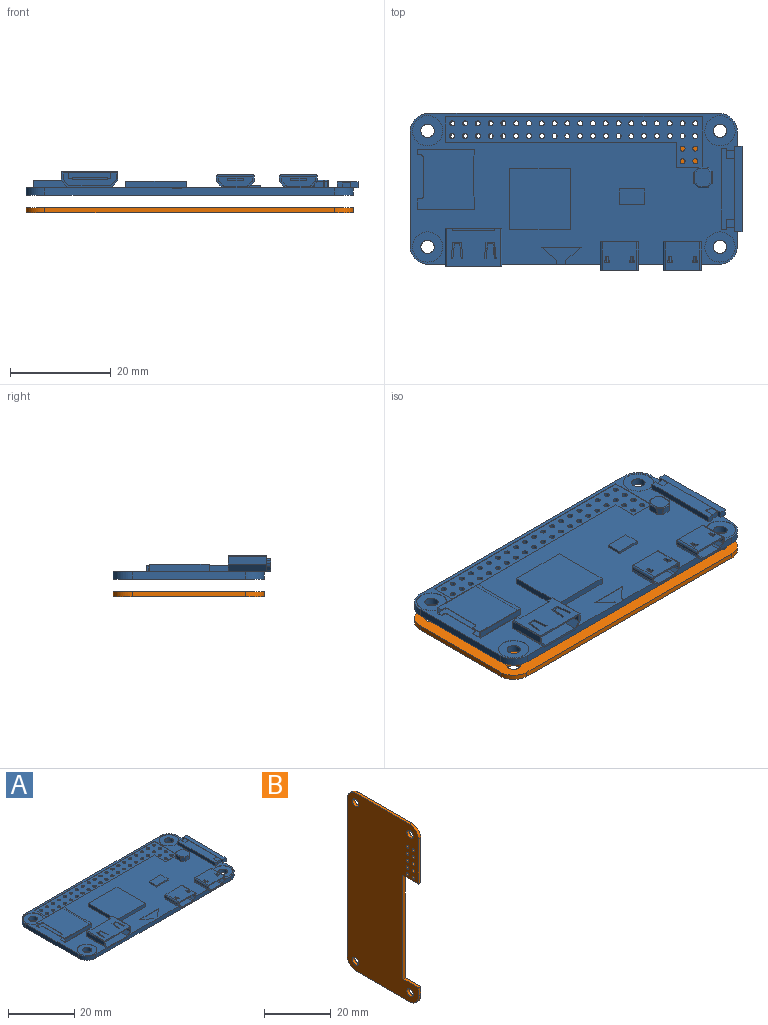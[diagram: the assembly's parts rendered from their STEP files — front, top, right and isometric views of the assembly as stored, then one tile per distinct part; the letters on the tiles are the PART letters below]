
ASSEMBLY  parts=2 mates=1
PART A: 316 faces, bbox 65.9x31.3x4.8 mm
  f0: plane 8.42x0.4mm, normal (0,0,-1), area 3.4mm2, adj f8,f9,f10,f121
  f1: plane 10.55x2.6mm, normal (0,-1,0), area 22.2mm2, adj f15,f16,f17,f18,f19,f20,f21,f22
  f2: plane 7.6x1.57mm, normal (-1,0,0), area 12mm2, adj f7,f8,f11,f13
  f3: plane 10.85x7.6mm, normal (0,0,1), area 72.9mm2, adj f7,f8,f13,f14,f26,f27,f28,f29
  f4: plane 7.6x1.57mm, normal (1,0,0), area 12mm2, adj f7,f8,f12,f14
  f5: plane 7.6x1.33mm, normal (0.74,0,-0.67), area 13.7mm2, adj f7,f8,f9,f12
  f6: plane 7.6x1.33mm, normal (-0.74,0,-0.67), area 13.7mm2, adj f7,f8,f10,f11
  f7: plane 11.25x3.3mm, normal (0,1,0), area 23.4mm2, adj f2,f3,f4,f5,f6,f9,f10,f11
  f8: plane 11.25x3.3mm, normal (0,-1,0), area 9.1mm2, adj f0,f2,f3,f4,f5,f6,f9,f10
  f9: cylinder r=0.2mm len=7.6mm, axis (0,-1,0), area 1.3mm2, adj f0,f5,f7,f8,f98
  f10: cylinder r=0.2mm len=7.6mm, axis (0,-1,0), area 1.3mm2, adj f0,f6,f7,f8,f98
  f11: cylinder r=0.2mm len=7.6mm, axis (0,-1,0), area 1.1mm2, adj f2,f6,f7,f8
  f12: cylinder r=0.2mm len=7.6mm, axis (0,-1,0), area 1.1mm2, adj f4,f5,f7,f8
  f13: cylinder r=0.2mm len=7.6mm, axis (0,-1,0), area 2.4mm2, adj f2,f3,f7,f8
  f14: cylinder r=0.2mm len=7.6mm, axis (0,-1,0), area 2.4mm2, adj f3,f4,f7,f8
  f15: plane 10.55x7mm, normal (0,0,-1), area 68.5mm2, adj f1,f8,f16,f20,f26,f27,f28,f29
  f16: plane 7x1.36mm, normal (-1,0,0), area 9.5mm2, adj f1,f8,f15,f17
  f17: plane 7x1.24mm, normal (-0.74,0,0.67), area 11.7mm2, adj f1,f8,f16,f18
  f18: plane 8.29x7mm, normal (0,0,1), area 58mm2, adj f1,f8,f17,f19
  f19: plane 7x1.24mm, normal (0.74,0,0.67), area 11.7mm2, adj f1,f8,f18,f20
  f20: plane 7x1.36mm, normal (1,0,0), area 9.5mm2, adj f1,f8,f15,f19
  f21: plane 3.5x0.55mm, normal (-1,0,0), area 1.9mm2, adj f1,f22,f24,f25
  f22: plane 7x3.5mm, normal (0,0,-1), area 24.5mm2, adj f1,f21,f23,f25
  f23: plane 3.5x0.55mm, normal (1,0,0), area 1.9mm2, adj f1,f22,f24,f25
  f24: plane 7x3.5mm, normal (0,0,1), area 24.5mm2, adj f1,f21,f23,f25
  f25: plane 7x0.55mm, normal (0,-1,0), area 3.8mm2, adj f21,f22,f23,f24
  f26: plane 3.3x0.35mm, normal (-1,-0.1,0), area 1.2mm2, adj f3,f15,f27,f33
  f27: plane 1.7x0.35mm, normal (0,-1,0), area 0.6mm2, adj f3,f15,f26,f28
  f28: plane 3.3x0.35mm, normal (1,-0.1,0), area 1.2mm2, adj f3,f15,f27,f29
  f29: plane 0.35x0.35mm, normal (0,1,0), area 0.1mm2, adj f3,f15,f28,f30
  f30: plane 2.95x0.35mm, normal (-1,0.1,0), area 1mm2, adj f3,f15,f29,f31
  f31: plane 1.07x0.35mm, normal (0,1,0), area 0.4mm2, adj f3,f15,f30,f32
  f32: plane 2.95x0.35mm, normal (1,0.1,0), area 1mm2, adj f3,f15,f31,f33
  f33: plane 0.35x0.35mm, normal (0,1,0), area 0.1mm2, adj f3,f15,f26,f32
  f34: plane 1.7x0.35mm, normal (0,-1,0), area 0.6mm2, adj f3,f15,f35,f41
  f35: plane 3.3x0.35mm, normal (1,-0.1,0), area 1.2mm2, adj f3,f15,f34,f36
  f36: plane 0.35x0.35mm, normal (0,1,0), area 0.1mm2, adj f3,f15,f35,f37
  f37: plane 2.95x0.35mm, normal (-1,0.1,0), area 1mm2, adj f3,f15,f36,f38
  f38: plane 1.07x0.35mm, normal (0,1,0), area 0.4mm2, adj f3,f15,f37,f39
  f39: plane 2.95x0.35mm, normal (1,0.1,0), area 1mm2, adj f3,f15,f38,f40
  f40: plane 0.35x0.35mm, normal (0,1,0), area 0.1mm2, adj f3,f15,f39,f41
  f41: plane 3.3x0.35mm, normal (-1,-0.1,0), area 1.2mm2, adj f3,f15,f34,f40
  f42: plane 1.4x0.5mm, normal (-1,0,0), area 0.7mm2, adj f3,f7,f44,f45
  f43: plane 1.4x0.5mm, normal (1,0,0), area 0.7mm2, adj f3,f7,f44,f45
  f44: plane 8.4x0.5mm, normal (0,0,1), area 4.2mm2, adj f7,f42,f43,f45
  f45: plane 8.4x1.4mm, normal (0,1,0), area 11.8mm2, adj f3,f42,f43,f44
  f46: cylinder r=3mm len=6mm, axis (0,0,1), area 1.9mm2, adj f98,f137
  f47: cylinder r=3mm len=6mm, axis (0,0,1), area 1.9mm2, adj f98,f136
  f48: cylinder r=3mm len=6mm, axis (0,0,1), area 1.9mm2, adj f98,f135
  f49: cylinder r=3mm len=6mm, axis (0,0,1), area 1.9mm2, adj f98,f127
  f50: cylinder r=1.32mm len=2.65mm, axis (0,0,1), area 11.7mm2, adj f126,f127
  f51: cylinder r=0.5mm len=1.4mm, axis (0,0,1), area 4.4mm2, adj f126,f128
  f52: cylinder r=0.5mm len=1.4mm, axis (0,0,1), area 4.4mm2, adj f126,f128
  f53: cylinder r=0.5mm len=1.4mm, axis (0,0,1), area 4.4mm2, adj f126,f128
  f54: cylinder r=0.5mm len=1.4mm, axis (0,0,1), area 4.4mm2, adj f126,f128
  f55: cylinder r=0.5mm len=1.4mm, axis (0,0,1), area 4.4mm2, adj f126,f128
  f56: cylinder r=0.5mm len=1.4mm, axis (0,0,1), area 4.4mm2, adj f126,f128
  f57: cylinder r=0.5mm len=1.4mm, axis (0,0,1), area 4.4mm2, adj f126,f128
  f58: cylinder r=0.5mm len=1.4mm, axis (0,0,1), area 4.4mm2, adj f126,f128
  f59: cylinder r=1.32mm len=2.65mm, axis (0,0,1), area 11.7mm2, adj f126,f135
  f60: cylinder r=1.32mm len=2.65mm, axis (0,0,1), area 11.7mm2, adj f126,f136
  f61: cylinder r=1.32mm len=2.65mm, axis (0,0,1), area 11.7mm2, adj f126,f137
  f62: cylinder r=0.5mm len=1.4mm, axis (0,0,1), area 4.4mm2, adj f126,f128
  f63: cylinder r=0.5mm len=1.4mm, axis (0,0,1), area 4.4mm2, adj f126,f128
  f64: cylinder r=0.5mm len=1.4mm, axis (0,0,1), area 4.4mm2, adj f126,f128
  f65: cylinder r=0.5mm len=1.4mm, axis (0,0,1), area 4.4mm2, adj f126,f128
  f66: cylinder r=0.5mm len=1.4mm, axis (0,0,1), area 4.4mm2, adj f126,f128
  f67: cylinder r=0.5mm len=1.4mm, axis (0,0,1), area 4.4mm2, adj f126,f128
  f68: cylinder r=0.5mm len=1.4mm, axis (0,0,1), area 4.4mm2, adj f126,f128
  f69: cylinder r=0.5mm len=1.4mm, axis (0,0,1), area 4.4mm2, adj f126,f128
  f70: cylinder r=0.5mm len=1.4mm, axis (0,0,1), area 4.4mm2, adj f126,f128
  f71: cylinder r=0.5mm len=1.4mm, axis (0,0,1), area 4.4mm2, adj f126,f128
  f72: cylinder r=0.5mm len=1.4mm, axis (0,0,1), area 4.4mm2, adj f126,f128
  f73: cylinder r=0.5mm len=1.4mm, axis (0,0,1), area 4.4mm2, adj f126,f128
  f74: cylinder r=0.5mm len=1.4mm, axis (0,0,1), area 4.4mm2, adj f126,f128
  f75: cylinder r=0.5mm len=1.4mm, axis (0,0,1), area 4.4mm2, adj f126,f128
  f76: cylinder r=0.5mm len=1.4mm, axis (0,0,1), area 4.4mm2, adj f126,f128
  f77: cylinder r=0.5mm len=1.4mm, axis (0,0,1), area 4.4mm2, adj f126,f128
  f78: cylinder r=0.5mm len=1.4mm, axis (0,0,1), area 4.4mm2, adj f126,f128
  f79: cylinder r=0.5mm len=1.4mm, axis (0,0,1), area 4.4mm2, adj f126,f128
  f80: cylinder r=0.5mm len=1.4mm, axis (0,0,1), area 4.4mm2, adj f126,f128
  f81: cylinder r=0.5mm len=1.4mm, axis (0,0,1), area 4.4mm2, adj f126,f128
  f82: cylinder r=0.5mm len=1.4mm, axis (0,0,1), area 4.4mm2, adj f126,f128
  f83: cylinder r=0.5mm len=1.4mm, axis (0,0,1), area 4.4mm2, adj f126,f128
  f84: cylinder r=0.5mm len=1.4mm, axis (0,0,1), area 4.4mm2, adj f126,f128
  f85: cylinder r=0.5mm len=1.4mm, axis (0,0,1), area 4.4mm2, adj f126,f128
  f86: cylinder r=0.5mm len=1.4mm, axis (0,0,1), area 4.4mm2, adj f126,f128
  f87: cylinder r=0.5mm len=1.4mm, axis (0,0,1), area 4.4mm2, adj f126,f128
  f88: cylinder r=0.5mm len=1.4mm, axis (0,0,1), area 4.4mm2, adj f126,f128
  f89: cylinder r=0.5mm len=1.4mm, axis (0,0,1), area 4.4mm2, adj f126,f128
  f90: cylinder r=0.5mm len=1.4mm, axis (0,0,1), area 4.4mm2, adj f126,f128
  f91: cylinder r=0.5mm len=1.4mm, axis (0,0,1), area 4.4mm2, adj f126,f128
  f92: cylinder r=0.5mm len=1.4mm, axis (0,0,1), area 4.4mm2, adj f126,f128
  f93: cylinder r=0.5mm len=1.4mm, axis (0,0,1), area 4.4mm2, adj f126,f128
  f94: cylinder r=0.5mm len=1.4mm, axis (0,0,1), area 4.4mm2, adj f126,f128
  f95: cylinder r=0.5mm len=1.4mm, axis (0,0,1), area 4.4mm2, adj f126,f128
  f96: cylinder r=0.5mm len=1.4mm, axis (0,0,1), area 4.4mm2, adj f126,f128
  f97: cylinder r=0.5mm len=1.4mm, axis (0,0,1), area 4.4mm2, adj f126,f128
  f98: plane 65x30mm, normal (0,0,1), area 1077.1mm2, adj f7,f9,f10,f46,f47,f48,f49,f99
  f99: plane 17x1.2mm, normal (-1,0,0), area 2.7mm2, adj f98,f102,f258,f259,f260,f267,f268,f273
  f100: plane 2x1.19mm, normal (1,0,0), area 0.7mm2, adj f98,f267,f268,f269,f275,f276
  f101: plane 2x1.19mm, normal (1,0,0), area 0.7mm2, adj f98,f102,f267,f271,f273,f274
  f102: plane 1.6x0.19mm, normal (0,1,0), area 0.3mm2, adj f99,f101,f267,f274
  f103: plane 11.9x0.5mm, normal (0,0,1), area 6mm2, adj f123,f262,f264,f272
  f104: plane 6.91x1.96mm, normal (0,-1,0), area 11.2mm2, adj f204,f205,f206,f207,f208,f209,f210,f211
  f105: plane 6.91x1.96mm, normal (0,-1,0), area 11.2mm2, adj f192,f193,f194,f195,f196,f197,f198,f199
  f106: plane 1.45x1.1mm, normal (-1,0,0), area 0.3mm2, adj f98,f107,f108,f155,f156,f157,f159,f160
  f107: plane 0.65x0.1mm, normal (0,-1,0), area 0.1mm2, adj f98,f106,f109,f160
  f108: plane 0.65x0.1mm, normal (0,-1,0), area 0.1mm2, adj f106,f110,f156,f162
  f109: cylinder r=0.5mm len=0.5mm, axis (0,0,-1), area 0.1mm2, adj f98,f107,f111,f160
  f110: cylinder r=0.5mm len=0.5mm, axis (0,0,-1), area 0.1mm2, adj f108,f112,f156,f162
  f111: plane 7.75x0.1mm, normal (-1,0,0), area 0.8mm2, adj f98,f109,f113,f160
  f112: plane 7.75x0.1mm, normal (-1,0,0), area 0.8mm2, adj f110,f114,f156,f162
  f113: cylinder r=0.5mm len=0.5mm, axis (0,0,-1), area 0.1mm2, adj f98,f111,f115,f160
  f114: cylinder r=0.5mm len=0.5mm, axis (0,0,-1), area 0.1mm2, adj f112,f116,f156,f162
  f115: plane 0.65x0.1mm, normal (0,1,0), area 0.1mm2, adj f98,f113,f117,f160
  f116: plane 0.65x0.1mm, normal (0,1,0), area 0.1mm2, adj f114,f117,f156,f162
  f117: plane 2.15x1.45mm, normal (-1,0,0), area 0.6mm2, adj f98,f115,f116,f149,f156,f158,f160,f161
  f118: cylinder r=3.75mm len=3.75mm, axis (0,0,-1), area 8.8mm2, adj f98,f119,f125,f126
  f119: plane 22.5x1.5mm, normal (-1,0,0), area 33.8mm2, adj f98,f118,f120,f126
  f120: cylinder r=3.75mm len=3.75mm, axis (0,0,-1), area 8.8mm2, adj f98,f119,f121,f126
  f121: plane 57.5x1.5mm, normal (0,-1,0), area 86.1mm2, adj f0,f98,f120,f122,f126,f141,f142,f143
  f122: cylinder r=3.75mm len=3.75mm, axis (0,0,-1), area 8.8mm2, adj f98,f121,f123,f126
  f123: plane 22.5x1.5mm, normal (1,0,0), area 33.8mm2, adj f98,f103,f122,f124,f126,f261,f265
  f124: cylinder r=3.75mm len=3.75mm, axis (0,0,-1), area 8.8mm2, adj f98,f123,f125,f126
  f125: plane 57.5x1.5mm, normal (0,1,0), area 86.3mm2, adj f98,f118,f124,f126
  f126: plane 65x30mm, normal (0,0,-1), area 1881.3mm2, adj f50,f51,f52,f53,f54,f55,f56,f57
  f127: plane 6x6mm, normal (0,0,1), area 22.8mm2, adj f49,f50
  f128: plane 51x10.1mm, normal (0,0,1), area 251mm2, adj f51,f52,f53,f54,f55,f56,f57,f58
  f129: plane 5.1x0.1mm, normal (1,0,0), area 0.5mm2, adj f98,f128,f130,f134
  f130: plane 51x0.1mm, normal (0,-1,0), area 5.1mm2, adj f98,f128,f129,f131
  f131: plane 10.1x0.1mm, normal (-1,0,0), area 1mm2, adj f98,f128,f130,f132,f277
  f132: plane 5.1x0.1mm, normal (0,1,0), area 0.5mm2, adj f98,f128,f131,f133,f277
  f133: plane 5x0.1mm, normal (1,0,0), area 0.5mm2, adj f98,f128,f132,f134
  f134: plane 45.9x0.1mm, normal (0,1,0), area 4.6mm2, adj f98,f128,f129,f133
  f135: plane 6x6mm, normal (0,0,1), area 22.8mm2, adj f48,f59
  f136: plane 6x6mm, normal (0,0,1), area 22.8mm2, adj f47,f60
  f137: plane 6x6mm, normal (0,0,1), area 22.8mm2, adj f46,f61
  f138: plane 3.08x2.65mm, normal (0.65,0.76,0), area 0.4mm2, adj f98,f139,f142,f143
  f139: plane 8x0.1mm, normal (0,-1,0), area 0.8mm2, adj f98,f138,f140,f143
  f140: plane 3.08x2.65mm, normal (-0.65,0.76,0), area 0.4mm2, adj f98,f139,f141,f143
  f141: plane 0.8x0.1mm, normal (-1,0,0), area 0.1mm2, adj f98,f121,f140,f143
  f142: plane 0.8x0.1mm, normal (1,0,0), area 0.1mm2, adj f98,f121,f138,f143
  f143: plane 8x3.45mm, normal (0,0,1), area 14.5mm2, adj f121,f138,f139,f140,f141,f142
  f144: plane 12x1.25mm, normal (1,0,0), area 15mm2, adj f98,f145,f147,f148
  f145: plane 12x1.25mm, normal (0,1,0), area 15mm2, adj f98,f144,f146,f148
  f146: plane 12x1.25mm, normal (-1,0,0), area 15mm2, adj f98,f145,f147,f148
  f147: plane 12x1.25mm, normal (0,-1,0), area 15mm2, adj f98,f144,f146,f148
  f148: plane 12x12mm, normal (0,0,1), area 144mm2, adj f144,f145,f146,f147
  f149: plane 11.4x1.35mm, normal (0,-1,0), area 15.4mm2, adj f98,f117,f150,f158
  f150: plane 2.5x1.45mm, normal (1,0,0), area 3.6mm2, adj f98,f149,f151,f156,f158
  f151: plane 1.45x0.25mm, normal (0.71,0.71,0), area 0.5mm2, adj f98,f150,f152,f156
  f152: plane 7.9x1.45mm, normal (1,0,0), area 11.5mm2, adj f98,f151,f153,f156
  f153: plane 1.45x0.25mm, normal (0.71,-0.71,0), area 0.5mm2, adj f98,f152,f154,f156
  f154: plane 1.45x1.1mm, normal (1,0,0), area 1.6mm2, adj f98,f153,f155,f156,f157
  f155: plane 11.4x1.35mm, normal (0,1,0), area 15.4mm2, adj f98,f106,f154,f157
  f156: plane 11.8x11.4mm, normal (0,0,1), area 122.5mm2, adj f106,f108,f110,f112,f114,f116,f117,f150
  f157: cylinder r=0.1mm len=11.4mm, axis (-1,0,0), area 1.8mm2, adj f106,f154,f155,f156
  f158: cylinder r=0.1mm len=11.4mm, axis (1,0,0), area 1.8mm2, adj f117,f149,f150,f156
  f159: plane 10.65x1.25mm, normal (0,-1,0), area 13.3mm2, adj f106,f160,f162,f163
  f160: plane 11.8x10.65mm, normal (0,0,1), area 115.7mm2, adj f106,f107,f109,f111,f113,f115,f117,f159
  f161: plane 10.65x1.25mm, normal (0,1,0), area 13.3mm2, adj f117,f160,f162,f163
  f162: plane 11.8x10.65mm, normal (0,0,-1), area 115.7mm2, adj f106,f108,f110,f112,f114,f116,f117,f159
  f163: plane 11.8x1.25mm, normal (-1,0,0), area 14.7mm2, adj f159,f160,f161,f162
  f164: plane 4.3x1.25mm, normal (0,0,-1), area 5.4mm2, adj f121,f165,f166,f177
  f165: cylinder r=1mm len=5.75mm, axis (0,-1,0), area 4.6mm2, adj f98,f164,f175,f176,f177
  f166: cylinder r=1mm len=5.75mm, axis (0,-1,0), area 4.6mm2, adj f98,f164,f167,f176,f177
  f167: plane 5.75x0.65mm, normal (-0.72,0,-0.69), area 5.2mm2, adj f166,f168,f176,f177
  f168: cylinder r=1mm len=5.75mm, axis (0,-1,0), area 4.4mm2, adj f167,f169,f176,f177
  f169: plane 5.75x0.55mm, normal (-1,0,0), area 3.1mm2, adj f168,f170,f176,f177
  f170: cylinder r=0.4mm len=5.75mm, axis (0,-1,0), area 3.6mm2, adj f169,f171,f176,f177
  f171: plane 6.75x5.75mm, normal (0,0,1), area 36.8mm2, adj f170,f172,f176,f177,f234,f235,f236,f237
  f172: cylinder r=0.4mm len=5.75mm, axis (0,-1,0), area 3.6mm2, adj f171,f173,f176,f177
  f173: plane 5.75x0.55mm, normal (1,0,0), area 3.1mm2, adj f172,f174,f176,f177
  f174: cylinder r=1mm len=5.75mm, axis (0,-1,0), area 4.4mm2, adj f173,f175,f176,f177
  f175: plane 5.75x0.65mm, normal (0.72,0,-0.69), area 5.2mm2, adj f165,f174,f176,f177
  f176: plane 7.55x2.6mm, normal (0,1,0), area 18mm2, adj f98,f165,f166,f167,f168,f169,f170,f171
  f177: plane 7.55x2.6mm, normal (0,-1,0), area 5.6mm2, adj f164,f165,f166,f167,f168,f169,f170,f171
  f178: plane 4.3x1.25mm, normal (0,0,-1), area 5.4mm2, adj f121,f183,f184,f191
  f179: cylinder r=0.4mm len=5.75mm, axis (0,-1,0), area 3.6mm2, adj f180,f189,f190,f191
  f180: plane 5.75x0.55mm, normal (1,0,0), area 3.1mm2, adj f179,f181,f190,f191
  f181: cylinder r=1mm len=5.75mm, axis (0,-1,0), area 4.4mm2, adj f180,f182,f190,f191
  f182: plane 5.75x0.65mm, normal (0.72,0,-0.69), area 5.2mm2, adj f181,f183,f190,f191
  f183: cylinder r=1mm len=5.75mm, axis (0,-1,0), area 4.6mm2, adj f98,f178,f182,f190,f191
  f184: cylinder r=1mm len=5.75mm, axis (0,-1,0), area 4.6mm2, adj f98,f178,f185,f190,f191
  f185: plane 5.75x0.65mm, normal (-0.72,0,-0.69), area 5.2mm2, adj f184,f186,f190,f191
  f186: cylinder r=1mm len=5.75mm, axis (0,-1,0), area 4.4mm2, adj f185,f187,f190,f191
  f187: plane 5.75x0.55mm, normal (-1,0,0), area 3.1mm2, adj f186,f188,f190,f191
  f188: cylinder r=0.4mm len=5.75mm, axis (0,-1,0), area 3.6mm2, adj f187,f189,f190,f191
  f189: plane 6.75x5.75mm, normal (0,0,1), area 36.8mm2, adj f179,f188,f190,f191,f226,f227,f228,f229
  f190: plane 7.55x2.6mm, normal (0,1,0), area 18mm2, adj f98,f179,f180,f181,f182,f183,f184,f185
  f191: plane 7.55x2.6mm, normal (0,-1,0), area 5.6mm2, adj f178,f179,f180,f181,f182,f183,f184,f185
  f192: cylinder r=0.08mm len=5.25mm, axis (0,-1,0), area 0.7mm2, adj f105,f191,f193,f203
  f193: plane 5.25x0.55mm, normal (-1,0,0), area 2.9mm2, adj f105,f191,f192,f194
  f194: cylinder r=0.68mm len=5.25mm, axis (0,-1,0), area 2.7mm2, adj f105,f191,f193,f195
  f195: plane 5.25x0.65mm, normal (-0.72,0,0.69), area 4.7mm2, adj f105,f191,f194,f196
  f196: cylinder r=0.68mm len=5.25mm, axis (0,-1,0), area 2.9mm2, adj f105,f191,f195,f197
  f197: plane 5.25x4.3mm, normal (0,0,1), area 22.6mm2, adj f105,f191,f196,f198
  f198: cylinder r=0.68mm len=5.25mm, axis (0,-1,0), area 2.9mm2, adj f105,f191,f197,f199
  f199: plane 5.25x0.65mm, normal (0.72,0,0.69), area 4.7mm2, adj f105,f191,f198,f200
  f200: cylinder r=0.68mm len=5.25mm, axis (0,-1,0), area 2.7mm2, adj f105,f191,f199,f201
  f201: plane 5.25x0.55mm, normal (1,0,0), area 2.9mm2, adj f105,f191,f200,f202
  f202: cylinder r=0.08mm len=5.25mm, axis (0,-1,0), area 0.7mm2, adj f105,f191,f201,f203
  f203: plane 6.75x5.25mm, normal (0,0,-1), area 33.4mm2, adj f105,f191,f192,f202,f226,f227,f228,f229
  f204: cylinder r=0.68mm len=5.25mm, axis (0,-1,0), area 2.9mm2, adj f104,f177,f205,f215
  f205: plane 5.25x4.3mm, normal (0,0,1), area 22.6mm2, adj f104,f177,f204,f206
  f206: cylinder r=0.68mm len=5.25mm, axis (0,-1,0), area 2.9mm2, adj f104,f177,f205,f207
  f207: plane 5.25x0.65mm, normal (0.72,0,0.69), area 4.7mm2, adj f104,f177,f206,f208
  f208: cylinder r=0.68mm len=5.25mm, axis (0,-1,0), area 2.7mm2, adj f104,f177,f207,f209
  f209: plane 5.25x0.55mm, normal (1,0,0), area 2.9mm2, adj f104,f177,f208,f210
  f210: cylinder r=0.08mm len=5.25mm, axis (0,-1,0), area 0.7mm2, adj f104,f177,f209,f211
  f211: plane 6.75x5.25mm, normal (0,0,-1), area 33.4mm2, adj f104,f177,f210,f212,f234,f235,f236,f237
  f212: cylinder r=0.08mm len=5.25mm, axis (0,-1,0), area 0.7mm2, adj f104,f177,f211,f213
  f213: plane 5.25x0.55mm, normal (-1,0,0), area 2.9mm2, adj f104,f177,f212,f214
  f214: cylinder r=0.68mm len=5.25mm, axis (0,-1,0), area 2.7mm2, adj f104,f177,f213,f215
  f215: plane 5.25x0.65mm, normal (-0.72,0,0.69), area 4.7mm2, adj f104,f177,f204,f214
  f216: plane 3.5x0.4mm, normal (1,0,0), area 1.4mm2, adj f105,f217,f219,f220
  f217: plane 3.5x3.15mm, normal (0,0,1), area 11mm2, adj f105,f216,f218,f220
  f218: plane 3.5x0.4mm, normal (-1,0,0), area 1.4mm2, adj f105,f217,f219,f220
  f219: plane 3.5x3.15mm, normal (0,0,-1), area 11mm2, adj f105,f216,f218,f220
  f220: plane 3.15x0.4mm, normal (0,-1,0), area 1.3mm2, adj f216,f217,f218,f219
  f221: plane 3.5x0.4mm, normal (1,0,0), area 1.4mm2, adj f104,f222,f224,f225
  f222: plane 3.5x3.15mm, normal (0,0,1), area 11mm2, adj f104,f221,f223,f225
  f223: plane 3.5x0.4mm, normal (-1,0,0), area 1.4mm2, adj f104,f222,f224,f225
  f224: plane 3.5x3.15mm, normal (0,0,-1), area 11mm2, adj f104,f221,f223,f225
  f225: plane 3.15x0.4mm, normal (0,-1,0), area 1.3mm2, adj f221,f222,f223,f224
  f226: plane 0.45x0.32mm, normal (-1,0,0), area 0.1mm2, adj f189,f203,f227,f233
  f227: plane 1.05x0.32mm, normal (0,1,0), area 0.3mm2, adj f189,f203,f226,f228
  f228: plane 0.45x0.32mm, normal (1,0,0), area 0.1mm2, adj f189,f203,f227,f229
  f229: plane 0.32x0.23mm, normal (0,-1,0), area 0.1mm2, adj f189,f203,f228,f230
  f230: plane 0.9x0.32mm, normal (1,0,0), area 0.3mm2, adj f189,f203,f229,f231
  f231: plane 0.6x0.32mm, normal (0,-1,0), area 0.2mm2, adj f189,f203,f230,f232
  f232: plane 0.9x0.32mm, normal (-1,0,0), area 0.3mm2, adj f189,f203,f231,f233
  f233: plane 0.32x0.23mm, normal (0,-1,0), area 0.1mm2, adj f189,f203,f226,f232
  f234: plane 0.6x0.32mm, normal (0,-1,0), area 0.2mm2, adj f171,f211,f235,f241
  f235: plane 0.9x0.32mm, normal (-1,0,0), area 0.3mm2, adj f171,f211,f234,f236
  f236: plane 0.32x0.23mm, normal (0,-1,0), area 0.1mm2, adj f171,f211,f235,f237
  f237: plane 0.45x0.32mm, normal (-1,0,0), area 0.1mm2, adj f171,f211,f236,f238
  f238: plane 1.05x0.32mm, normal (0,1,0), area 0.3mm2, adj f171,f211,f237,f239
  f239: plane 0.45x0.32mm, normal (1,0,0), area 0.1mm2, adj f171,f211,f238,f240
  f240: plane 0.32x0.23mm, normal (0,-1,0), area 0.1mm2, adj f171,f211,f239,f241
  f241: plane 0.9x0.32mm, normal (1,0,0), area 0.3mm2, adj f171,f211,f234,f240
  f242: plane 0.9x0.32mm, normal (-1,0,0), area 0.3mm2, adj f171,f211,f243,f249
  f243: plane 0.32x0.23mm, normal (0,-1,0), area 0.1mm2, adj f171,f211,f242,f244
  f244: plane 0.45x0.32mm, normal (-1,0,0), area 0.1mm2, adj f171,f211,f243,f245
  f245: plane 1.05x0.32mm, normal (0,1,0), area 0.3mm2, adj f171,f211,f244,f246
  f246: plane 0.45x0.32mm, normal (1,0,0), area 0.1mm2, adj f171,f211,f245,f247
  f247: plane 0.32x0.23mm, normal (0,-1,0), area 0.1mm2, adj f171,f211,f246,f248
  f248: plane 0.9x0.32mm, normal (1,0,0), area 0.3mm2, adj f171,f211,f247,f249
  f249: plane 0.6x0.32mm, normal (0,-1,0), area 0.2mm2, adj f171,f211,f242,f248
  f250: plane 0.6x0.32mm, normal (0,-1,0), area 0.2mm2, adj f189,f203,f251,f257
  f251: plane 0.9x0.32mm, normal (-1,0,0), area 0.3mm2, adj f189,f203,f250,f252
  f252: plane 0.32x0.23mm, normal (0,-1,0), area 0.1mm2, adj f189,f203,f251,f253
  f253: plane 0.45x0.32mm, normal (-1,0,0), area 0.1mm2, adj f189,f203,f252,f254
  f254: plane 1.05x0.32mm, normal (0,1,0), area 0.3mm2, adj f189,f203,f253,f255
  f255: plane 0.45x0.32mm, normal (1,0,0), area 0.1mm2, adj f189,f203,f254,f256
  f256: plane 0.32x0.23mm, normal (0,-1,0), area 0.1mm2, adj f189,f203,f255,f257
  f257: plane 0.9x0.32mm, normal (1,0,0), area 0.3mm2, adj f189,f203,f250,f256
  f258: plane 1.4x1.2mm, normal (0,-1,0), area 1.7mm2, adj f98,f99,f259,f265,f266
  f259: plane 17x1.4mm, normal (0,0,1), area 23.8mm2, adj f99,f258,f260,f266
  f260: plane 1.4x1.2mm, normal (0,1,0), area 1.7mm2, adj f98,f99,f259,f261,f266
  f261: plane 2.55x0.9mm, normal (0,0,-1), area 2.3mm2, adj f123,f260,f262,f266
  f262: plane 1.4x0.65mm, normal (0,-1,0), area 0.9mm2, adj f103,f261,f263,f266,f272
  f263: plane 11.9x1.4mm, normal (0,0,-1), area 16.7mm2, adj f262,f264,f266,f272
  f264: plane 1.4x0.65mm, normal (0,1,0), area 0.9mm2, adj f103,f263,f265,f266,f272
  f265: plane 2.55x0.9mm, normal (0,0,-1), area 2.3mm2, adj f123,f258,f264,f266
  f266: plane 17x1.2mm, normal (1,0,0), area 12.7mm2, adj f258,f259,f260,f261,f262,f263,f264,f265
  f267: plane 16x2.7mm, normal (0,0,1), area 36.8mm2, adj f99,f100,f101,f102,f268,f269,f270,f271
  f268: plane 1.6x0.19mm, normal (0,-1,0), area 0.3mm2, adj f99,f100,f267,f276
  f269: plane 1.19x1.1mm, normal (0,-1,0), area 1.3mm2, adj f98,f100,f267,f270
  f270: plane 16x1.19mm, normal (-1,0,0), area 19mm2, adj f98,f267,f269,f271
  f271: plane 1.19x1.1mm, normal (0,1,0), area 1.3mm2, adj f98,f101,f267,f270
  f272: plane 11.9x0.65mm, normal (1,0,0), area 7.7mm2, adj f103,f262,f263,f264
  f273: plane 1.6x1mm, normal (0,1,0), area 1.6mm2, adj f98,f99,f101,f274
  f274: plane 1.7x1.6mm, normal (0,0,1), area 2.7mm2, adj f99,f101,f102,f273
  f275: plane 1.6x1mm, normal (0,-1,0), area 1.6mm2, adj f98,f99,f100,f276
  f276: plane 1.7x1.6mm, normal (0,0,1), area 2.7mm2, adj f99,f100,f268,f275
  f277: plane 0.8x0.05mm, normal (0,0,-1), area 0mm2, adj f131,f132,f281,f306
  f278: plane 2.03x1.3mm, normal (-1,0,0), area 2.6mm2, adj f98,f294,f299,f300
  f279: plane 1.68x1.3mm, normal (0,-1,0), area 2.2mm2, adj f98,f292,f297,f298
  f280: plane 2.03x1.3mm, normal (1,0,0), area 2.6mm2, adj f98,f303,f309,f310
  f281: plane 1.68x1.3mm, normal (0,1,0), area 2.2mm2, adj f98,f277,f306,f311,f312
  f282: plane 3.6x3.25mm, normal (0,0,1), area 10.5mm2, adj f293,f298,f299,f304,f305,f310,f311,f315
  f283: plane 1.3x0.78mm, normal (-0.71,0.71,0), area 1.4mm2, adj f98,f300,f305,f306
  f284: plane 1.3x0.78mm, normal (0.71,0.71,0), area 1.4mm2, adj f98,f309,f312,f315
  f285: plane 1.3x0.78mm, normal (0.71,-0.71,0), area 1.4mm2, adj f98,f297,f303,f304
  f286: plane 1.3x0.78mm, normal (-0.71,-0.71,0), area 1.4mm2, adj f98,f292,f293,f294
  f287: plane 3.15x0.5mm, normal (-1,0,0), area 1.6mm2, adj f98,f288,f290,f291
  f288: plane 5x0.5mm, normal (0,-1,0), area 2.5mm2, adj f98,f287,f289,f291
  f289: plane 3.15x0.5mm, normal (1,0,0), area 1.6mm2, adj f98,f288,f290,f291
  f290: plane 5x0.5mm, normal (0,1,0), area 2.5mm2, adj f98,f287,f289,f291
  f291: plane 5x3.15mm, normal (0,0,1), area 15.7mm2, adj f287,f288,f289,f290
  f292: cylinder r=0.2mm len=1.3mm, axis (0,0,-1), area 0.2mm2, adj f98,f279,f286,f295
  f293: cylinder r=0.2mm len=0.92mm, axis (-0.71,0.71,0), area 0.3mm2, adj f282,f286,f295,f296
  f294: cylinder r=0.2mm len=1.3mm, axis (0,0,1), area 0.2mm2, adj f98,f278,f286,f296
  f295: sphere r=0.2mm, area 0mm2, adj f292,f293,f298
  f296: sphere r=0.2mm, area 0mm2, adj f293,f294,f299
  f297: cylinder r=0.2mm len=1.3mm, axis (0,0,1), area 0.2mm2, adj f98,f279,f285,f301
  f298: cylinder r=0.2mm len=1.68mm, axis (-1,0,0), area 0.5mm2, adj f279,f282,f295,f301
  f299: cylinder r=0.2mm len=2.03mm, axis (0,1,0), area 0.6mm2, adj f278,f282,f296,f302
  f300: cylinder r=0.2mm len=1.3mm, axis (0,0,-1), area 0.2mm2, adj f98,f278,f283,f302
  f301: sphere r=0.2mm, area 0mm2, adj f297,f298,f304
  f302: sphere r=0.2mm, area 0mm2, adj f299,f300,f305
  f303: cylinder r=0.2mm len=1.3mm, axis (0,0,-1), area 0.2mm2, adj f98,f280,f285,f307
  f304: cylinder r=0.2mm len=0.92mm, axis (-0.71,-0.71,0), area 0.3mm2, adj f282,f285,f301,f307
  f305: cylinder r=0.2mm len=0.92mm, axis (0.71,0.71,0), area 0.3mm2, adj f282,f283,f302,f308
  f306: cylinder r=0.2mm len=1.3mm, axis (0,0,1), area 0.2mm2, adj f98,f277,f281,f283,f308
  f307: sphere r=0.2mm, area 0mm2, adj f303,f304,f310
  f308: sphere r=0.2mm, area 0mm2, adj f305,f306,f311
  f309: cylinder r=0.2mm len=1.3mm, axis (0,0,1), area 0.2mm2, adj f98,f280,f284,f313
  f310: cylinder r=0.2mm len=2.03mm, axis (0,-1,0), area 0.6mm2, adj f280,f282,f307,f313
  f311: cylinder r=0.2mm len=1.68mm, axis (1,0,0), area 0.5mm2, adj f281,f282,f308,f314
  f312: cylinder r=0.2mm len=1.3mm, axis (0,0,-1), area 0.2mm2, adj f98,f281,f284,f314
  f313: sphere r=0.2mm, area 0mm2, adj f309,f310,f315
  f314: sphere r=0.2mm, area 0mm2, adj f311,f312,f315
  f315: cylinder r=0.2mm len=0.92mm, axis (0.71,-0.71,0), area 0.3mm2, adj f282,f284,f313,f314
PART B: 28 faces, bbox 1x30x65 mm
  f0: plane 16.28x1mm, normal (0,-1,0), area 16.3mm2, adj f1,f2,f10,f11
  f1: plane 65x30mm, normal (1,0,0), area 1661.2mm2, adj f0,f3,f4,f5,f6,f7,f8,f9
  f2: plane 65x30mm, normal (-1,0,0), area 1661.2mm2, adj f0,f3,f4,f5,f6,f7,f8,f9
  f3: plane 3.25x1mm, normal (0,-1,0), area 3.3mm2, adj f1,f2,f4,f12
  f4: cylinder r=3.75mm len=3.75mm, axis (-1,0,0), area 5.9mm2, adj f1,f2,f3,f5
  f5: plane 22.5x1mm, normal (0,0,-1), area 22.5mm2, adj f1,f2,f4,f6
  f6: cylinder r=3.75mm len=3.75mm, axis (-1,0,0), area 5.9mm2, adj f1,f2,f5,f7
  f7: plane 57.5x1mm, normal (0,1,0), area 57.5mm2, adj f1,f2,f6,f8
  f8: cylinder r=3.75mm len=3.75mm, axis (-1,0,0), area 5.9mm2, adj f1,f2,f7,f9
  f9: plane 22.5x1mm, normal (0,0,1), area 22.5mm2, adj f1,f2,f8,f10
  f10: cylinder r=3.75mm len=3.75mm, axis (-1,0,0), area 5.9mm2, adj f0,f1,f2,f9
  f11: plane 6.5x1mm, normal (0,0,-1), area 6.5mm2, adj f0,f1,f2,f13
  f12: plane 6.5x1mm, normal (0,0,1), area 6.5mm2, adj f1,f2,f3,f13
  f13: plane 37.97x1mm, normal (0,-1,0), area 38mm2, adj f1,f2,f11,f12
  f14: cylinder r=1.32mm len=2.65mm, axis (1,0,0), area 8.3mm2, adj f1,f2
  f15: cylinder r=1.32mm len=2.65mm, axis (1,0,0), area 8.3mm2, adj f1,f2
  f16: cylinder r=1.32mm len=2.65mm, axis (1,0,0), area 8.3mm2, adj f1,f2
  f17: cylinder r=1.32mm len=2.65mm, axis (1,0,0), area 8.3mm2, adj f1,f2
  f18: cylinder r=0.5mm len=1mm, axis (1,0,0), area 3.1mm2, adj f1,f2
  f19: cylinder r=0.5mm len=1mm, axis (1,0,0), area 3.1mm2, adj f1,f2
  f20: cylinder r=0.5mm len=1mm, axis (1,0,0), area 3.1mm2, adj f1,f2
  f21: cylinder r=0.5mm len=1mm, axis (1,0,0), area 3.1mm2, adj f1,f2
  f22: cylinder r=0.5mm len=1mm, axis (1,0,0), area 3.1mm2, adj f1,f2
  f23: cylinder r=0.5mm len=1mm, axis (1,0,0), area 3.1mm2, adj f1,f2
  f24: cylinder r=0.5mm len=1mm, axis (1,0,0), area 3.1mm2, adj f1,f2
  f25: cylinder r=0.5mm len=1mm, axis (1,0,0), area 3.1mm2, adj f1,f2
  f26: cylinder r=0.5mm len=1mm, axis (1,0,0), area 3.1mm2, adj f1,f2
  f27: cylinder r=0.5mm len=1mm, axis (1,0,0), area 3.1mm2, adj f1,f2
PLACE A t=(30.9,17.32,-4.5)mm
PLACE B rot(axis=(0.71,0,-0.71),180deg) t=(30.89,17.33,-7)mm
MATE fastened B.f16 <-> A.f49  axis (0,0,1) through (1.87,28.85,-7)mm
